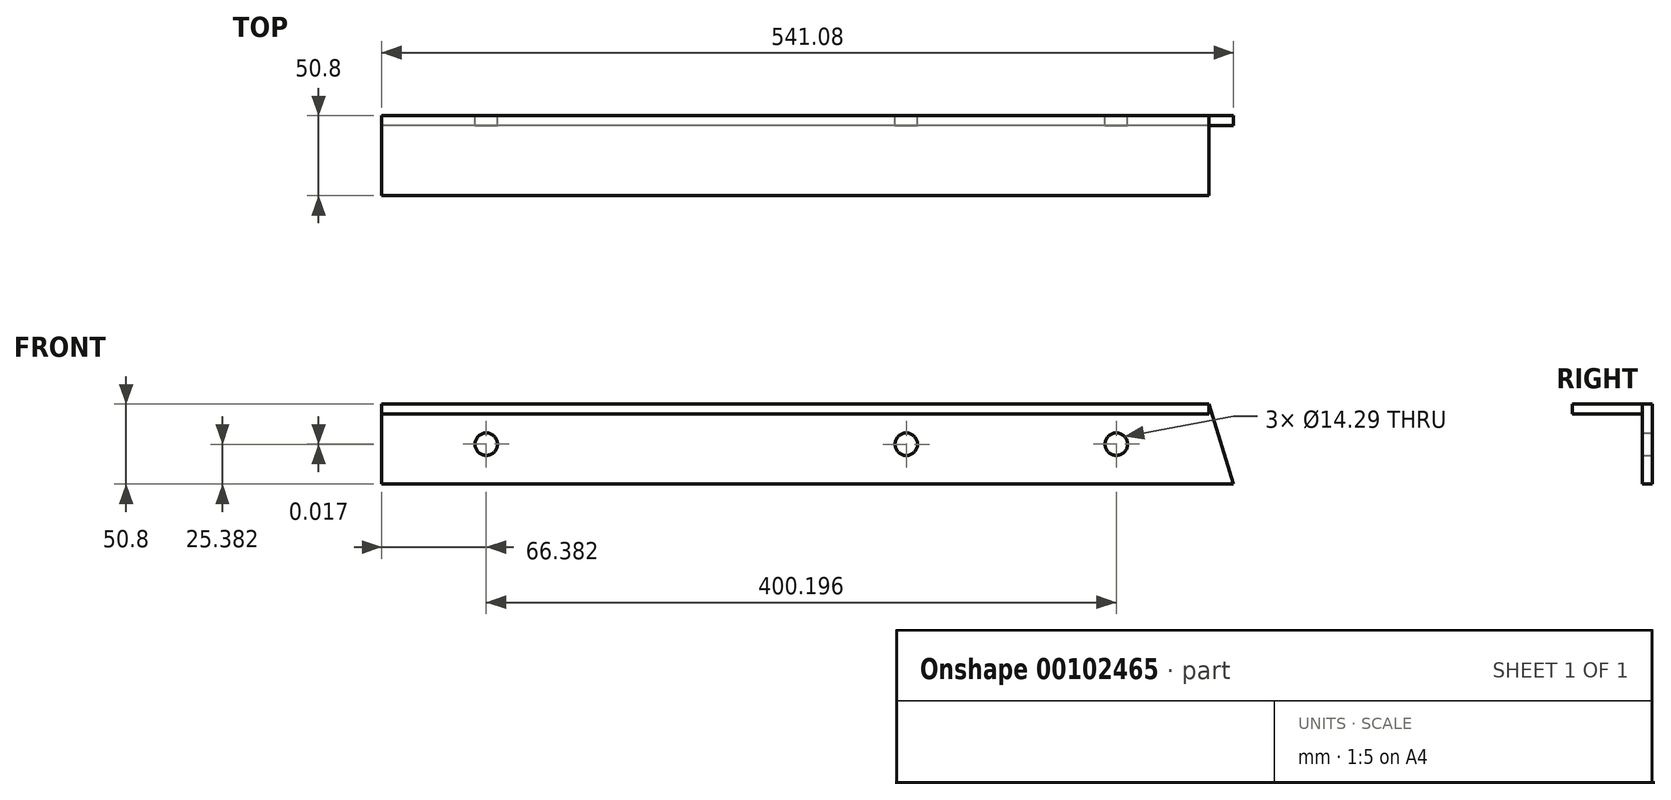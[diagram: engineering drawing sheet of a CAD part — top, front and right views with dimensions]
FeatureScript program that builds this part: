
annotation { "Feature Type Name" : "Feature", "Feature Type Description" : "" }
export const myFeature = defineFeature(function(context is Context, id is Id, definition is map)
    precondition{}
    {
        {
            var Q0;
            Q0=qCreatedBy(makeId("Front.planeOp"),FACE);
            var sketch = newSketch(context, id + "F0", { "sketchPlane" : qUnion([Q0])});
            skLineSegment(sketch, "E0", {"start": v(254.9, 25.4) * mm, "end": v(270.54, -25.4) * mm});
            skLineSegment(sketch, "E1", {"start": v(270.54, -25.4) * mm, "end": v(-270.54, -25.4) * mm});
            skLineSegment(sketch, "E2", {"start": v(-270.54, -25.4) * mm, "end": v(-270.54, 25.4) * mm});
            skLineSegment(sketch, "E3", {"start": v(-270.54, 25.4) * mm, "end": v(254.9, 25.4) * mm});
            skCircle(sketch, "E4", {"center": v(-204.16, 0) * mm, "radius": 7.14 * mm});
            skCircle(sketch, "E5", {"center": v(62.63, -0.02) * mm, "radius": 7.14 * mm});
            skCircle(sketch, "E6", {"center": v(196.04, 0) * mm, "radius": 7.14 * mm});
            skSolve(sketch);
        }
        {
            var Q0;
            Q0 = qSketchRegion(id + "F0", true);
            extrude(context, id + "F1", {"entities" : qUnion([Q0]), "depth" : 6.35 * mm});
        }
        {
            var Q0;
            Q0=makeQuery(id+"F1.opExtrude","CAP_FACE",FACE,{"disambiguationData":[OSD([sQuery(id+"F0.wireOp",EDGE,"E0"),sQuery(id+"F0.wireOp",EDGE,"E1"),sQuery(id+"F0.wireOp",EDGE,"E2"),sQuery(id+"F0.wireOp",EDGE,"E3"),sQuery(id+"F0.wireOp",EDGE,"E4"),sQuery(id+"F0.wireOp",EDGE,"E5"),sQuery(id+"F0.wireOp",EDGE,"E6")])],"isStart":false});
            var sketch = newSketch(context, id + "F2", { "sketchPlane" : qUnion([Q0])});
            skLineSegment(sketch, "E7", {"start": v(-270.54, 25.4) * mm, "end": v(254.9, 25.4) * mm});
            skLineSegment(sketch, "E8", {"start": v(254.9, 25.4) * mm, "end": v(254.9, 19.05) * mm});
            skLineSegment(sketch, "E9", {"start": v(254.9, 19.05) * mm, "end": v(-270.54, 19.05) * mm});
            skLineSegment(sketch, "E10", {"start": v(-270.54, 19.05) * mm, "end": v(-270.54, 25.4) * mm});
            skSolve(sketch);
        }
        {
            var Q0;
            Q0 = qSketchRegion(id + "F2", true);
            extrude(context, id + "F3", {"entities" : qUnion([Q0]), "operationType" : NewBodyOperationType.ADD, "depth" : 44.45 * mm});
        }
    });
